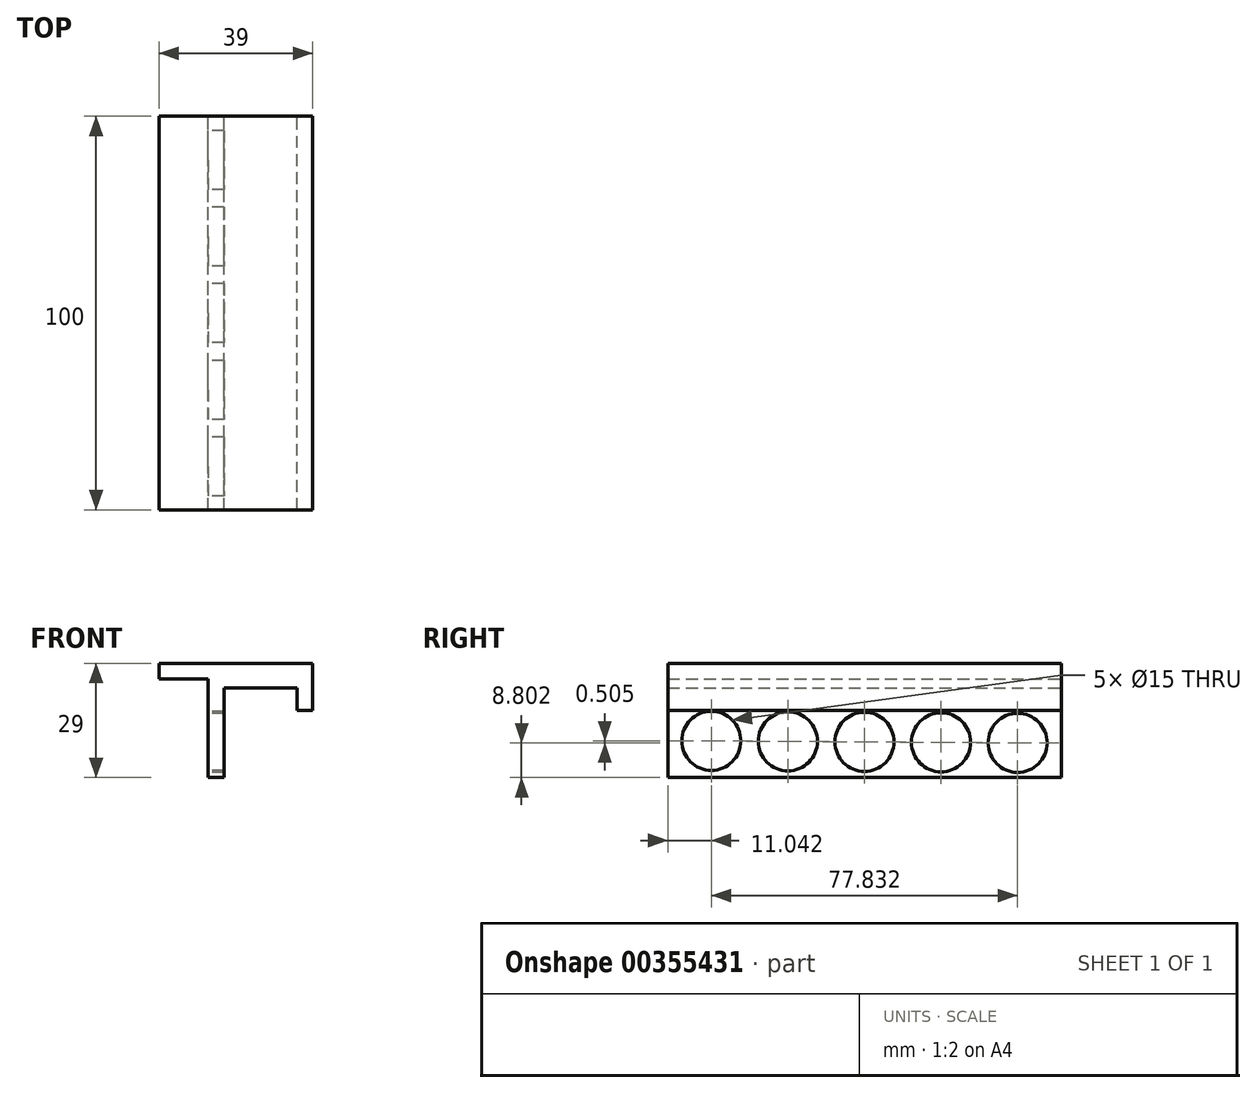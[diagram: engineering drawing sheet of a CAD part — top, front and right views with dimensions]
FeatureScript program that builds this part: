
annotation { "Feature Type Name" : "Feature", "Feature Type Description" : "" }
export const myFeature = defineFeature(function(context is Context, id is Id, definition is map)
    precondition{}
    {
        {
            var Q0;
            Q0=qCreatedBy(makeId("Front.planeOp"),FACE);
            var sketch = newSketch(context, id + "F0", { "sketchPlane" : qUnion([Q0])});
            skLineSegment(sketch, "E0", {"start": v(29.9, 18.12) * mm, "end": v(33.9, 18.12) * mm});
            skLineSegment(sketch, "E1", {"start": v(33.9, 18.12) * mm, "end": v(33.9, 26.12) * mm});
            skLineSegment(sketch, "E2", {"start": v(7.4, 26.12) * mm, "end": v(7.4, 1.12) * mm});
            skLineSegment(sketch, "E3", {"start": v(7.4, 1.12) * mm, "end": v(11.4, 1.12) * mm});
            skLineSegment(sketch, "E4", {"start": v(11.4, 1.12) * mm, "end": v(11.4, 23.88) * mm});
            skLineSegment(sketch, "E5", {"start": v(11.4, 23.88) * mm, "end": v(29.9, 23.88) * mm});
            skLineSegment(sketch, "E6", {"start": v(29.9, 23.88) * mm, "end": v(29.9, 18.12) * mm});
            skLineSegment(sketch, "E7.bottom", {"start": v(-5.1, 30.12) * mm, "end": v(33.9, 30.12) * mm});
            skLineSegment(sketch, "E7.top", {"start": v(-5.1, 26.12) * mm, "end": v(7.4, 26.12) * mm});
            skLineSegment(sketch, "E7.left", {"start": v(-5.1, 30.12) * mm, "end": v(-5.1, 26.12) * mm});
            skLineSegment(sketch, "E7.right", {"start": v(33.9, 30.12) * mm, "end": v(33.9, 26.12) * mm});
            skSolve(sketch);
        }
        {
            var Q0;
            Q0=makeQuery(id+"F0.imprint","IMPRINT",FACE,{"disambiguationData":[TD([[makeQuery(id+"F0.imprint","IMPRINT",EDGE,{"derivedFrom":sQuery(id+"F0.wireOp",EDGE,"E0")}),1.0]])]});
            extrude(context, id + "F1", {"entities" : qUnion([Q0]), "depth" : 100 * mm});
        }
        {
            var Q0;
            Q0=makeQuery(id+"F1.opExtrude","SWEPT_BODY",BODY,{"disambiguationData":[OSD([sQuery(id+"F0.wireOp",EDGE,"E0"),sQuery(id+"F0.wireOp",EDGE,"E1"),sQuery(id+"F0.wireOp",EDGE,"E2"),sQuery(id+"F0.wireOp",EDGE,"E3"),sQuery(id+"F0.wireOp",EDGE,"E4"),sQuery(id+"F0.wireOp",EDGE,"E5"),sQuery(id+"F0.wireOp",EDGE,"E6"),sQuery(id+"F0.wireOp",EDGE,"E7.bottom"),sQuery(id+"F0.wireOp",EDGE,"E7.top"),sQuery(id+"F0.wireOp",EDGE,"E7.left"),sQuery(id+"F0.wireOp",EDGE,"E7.right")])]});
            transform(context, id + "F2", {"entities" : qUnion([Q0]), "transformType" : TransformType.TRANSLATION_3D, "dx" : 0 * mm, "dy" : 46.4 * mm, "dz" : -0.6 * mm, "makeCopy" : false});
        }
        {
            var Q0;
            Q0=qCreatedBy(makeId("Right.planeOp"),FACE);
            var sketch = newSketch(context, id + "F3", { "sketchPlane" : qUnion([Q0])});
            skCircle(sketch, "E8", {"center": v(-42.56, 9.83) * mm, "radius": 4.56 * mm});
            skCircle(sketch, "E9.1.0.0", {"center": v(-23.1, 9.7) * mm, "radius": 4.56 * mm});
            skCircle(sketch, "E9.2.0.0", {"center": v(-3.64, 9.57) * mm, "radius": 4.56 * mm});
            skCircle(sketch, "E9.3.0.0", {"center": v(15.82, 9.45) * mm, "radius": 4.56 * mm});
            skCircle(sketch, "E9.4.0.0", {"center": v(35.27, 9.32) * mm, "radius": 4.56 * mm});
            skLineSegment(sketch, "E9.direction1", {"start": v(-42.56, 9.83) * mm, "end": v(-23.1, 9.7) * mm, "construction": true});
            skSolve(sketch);
        }
        {
            var Q0;
            Q0=sQuery(id+"F3.wireOp",VERTEX,"E9.4.0.0.center");
            var Q1;
            Q1=sQuery(id+"F3.wireOp",VERTEX,"E9.3.0.0.center");
            var Q2;
            Q2=sQuery(id+"F3.wireOp",VERTEX,"E9.2.0.0.center");
            var Q3;
            Q3=sQuery(id+"F3.wireOp",VERTEX,"E9.1.0.0.center");
            var Q4;
            Q4=sQuery(id+"F3.wireOp",VERTEX,"E9.direction1.start");
            var Q5;
            Q5=makeQuery(id+"F1.opExtrude","SWEPT_BODY",BODY,{"disambiguationData":[OSD([sQuery(id+"F0.wireOp",EDGE,"E0"),sQuery(id+"F0.wireOp",EDGE,"E1"),sQuery(id+"F0.wireOp",EDGE,"E2"),sQuery(id+"F0.wireOp",EDGE,"E3"),sQuery(id+"F0.wireOp",EDGE,"E4"),sQuery(id+"F0.wireOp",EDGE,"E5"),sQuery(id+"F0.wireOp",EDGE,"E6"),sQuery(id+"F0.wireOp",EDGE,"E7.bottom"),sQuery(id+"F0.wireOp",EDGE,"E7.top"),sQuery(id+"F0.wireOp",EDGE,"E7.left"),sQuery(id+"F0.wireOp",EDGE,"E7.right")])]});
            hole(context, id + "F4", {"style" : HoleStyle.SIMPLE, "endStyle" : HoleEndStyle.THROUGH, "oppositeDirection" : true, "holeDiameter" : 15 * mm, "isTappedThrough" : true, "tappedDepth" : 12 * mm, "tapClearance" : 3, "locations" : qUnion([Q0, Q1, Q2, Q3, Q4]), "scope" : qUnion([Q5])});
        }
    });
